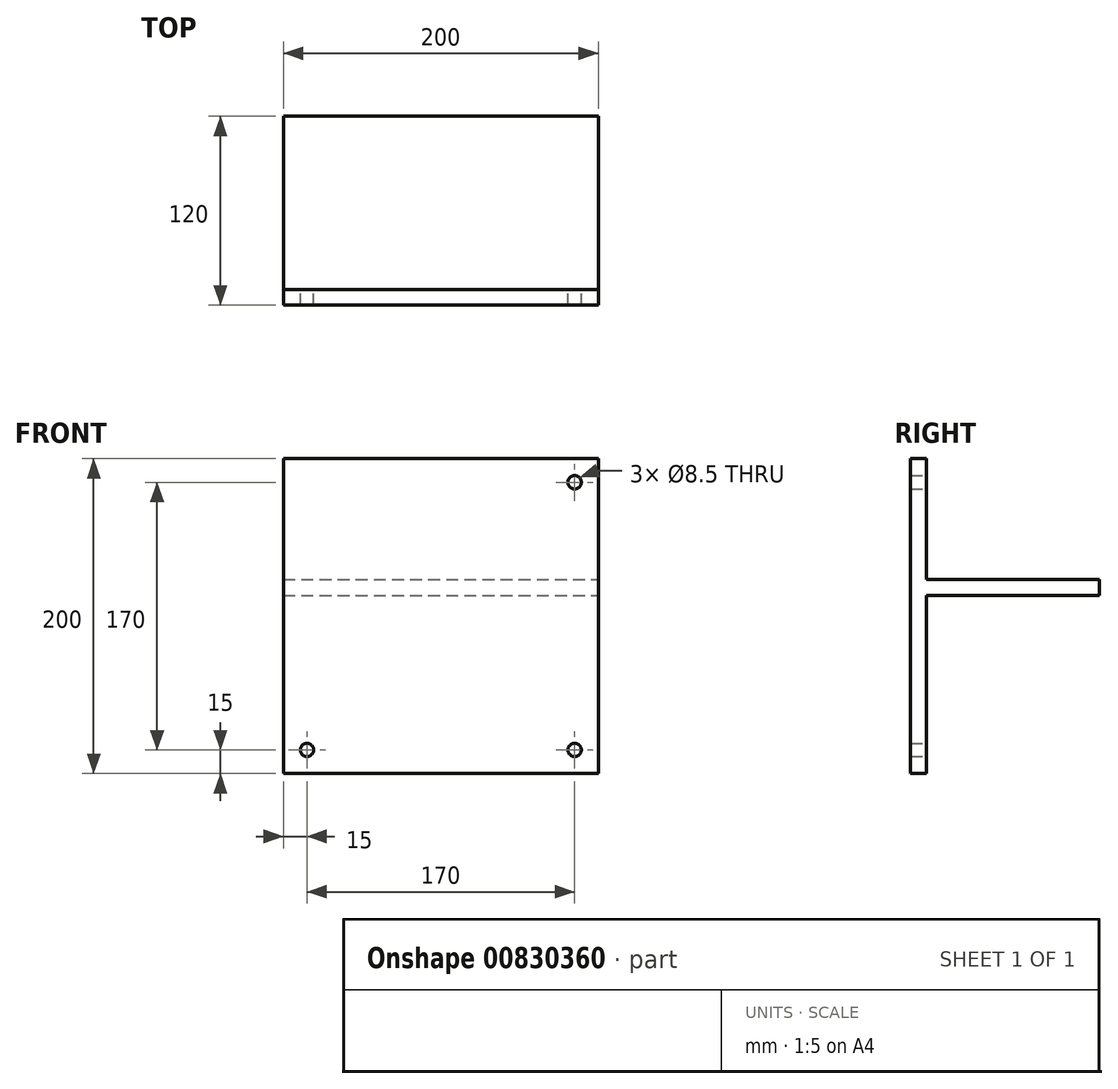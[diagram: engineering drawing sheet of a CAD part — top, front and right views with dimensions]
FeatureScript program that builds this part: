
annotation { "Feature Type Name" : "Feature", "Feature Type Description" : "" }
export const myFeature = defineFeature(function(context is Context, id is Id, definition is map)
    precondition{}
    {
        {
            var Q0;
            Q0=qCreatedBy(makeId("Front.planeOp"),FACE);
            var sketch = newSketch(context, id + "F0", { "sketchPlane" : qUnion([Q0])});
            skLineSegment(sketch, "E0.bottom", {"start": v(-100, 100) * mm, "end": v(100, 100) * mm});
            skLineSegment(sketch, "E0.top", {"start": v(-100, -100) * mm, "end": v(100, -100) * mm});
            skLineSegment(sketch, "E0.left", {"start": v(-100, 100) * mm, "end": v(-100, -100) * mm});
            skLineSegment(sketch, "E0.right", {"start": v(100, 100) * mm, "end": v(100, -100) * mm});
            skPoint(sketch, "E0.middle", {"position": v(0, 0) * mm});
            skSolve(sketch);
        }
        {
            var Q0;
            Q0=makeQuery(id+"F0.imprint","IMPRINT",FACE,{"disambiguationData":[TD([[makeQuery(id+"F0.imprint","IMPRINT",EDGE,{"derivedFrom":sQuery(id+"F0.wireOp",EDGE,"E0.bottom")}),-1.0]])]});
            extrude(context, id + "F1", {"entities" : qUnion([Q0]), "depth" : 120 * mm, "offsetDistance" : 25 * mm});
        }
        {
            var Q0;
            Q0=makeQuery(id+"F1.opExtrude","SWEPT_FACE",FACE,{"disambiguationData":[OSD([sQuery(id+"F0.wireOp",EDGE,"E0.right")])]});
            var sketch = newSketch(context, id + "F2", { "sketchPlane" : qUnion([Q0])});
            skLineSegment(sketch, "E1", {"start": v(-110, 100) * mm, "end": v(-110, -100) * mm});
            skLineSegment(sketch, "E2", {"start": v(-110, 23.2) * mm, "end": v(0, 23.2) * mm});
            skLineSegment(sketch, "E3", {"start": v(-110, 13.2) * mm, "end": v(0, 13.2) * mm});
            skSolve(sketch);
        }
        {
            var Q0;
            {var subQ4=sQuery(id+"F2.wireOp",EDGE,"E2");Q0=makeQuery(id+"F2.imprint","IMPRINT",FACE,{"disambiguationData":[TD([[makeQuery(id+"F2.imprint","IMPRINT",EDGE,{"derivedFrom":subQ4}),1.0]])]});}
            var Q1;
            {var subQ4=sQuery(id+"F2.wireOp",EDGE,"E3");Q1=makeQuery(id+"F2.imprint","IMPRINT",FACE,{"disambiguationData":[TD([[makeQuery(id+"F2.imprint","IMPRINT",EDGE,{"derivedFrom":subQ4}),-1.0]])]});}
            extrude(context, id + "F3", {"entities" : qUnion([Q0, Q1]), "operationType" : NewBodyOperationType.REMOVE, "oppositeDirection" : true, "depth" : 200 * mm, "offsetDistance" : 25 * mm});
        }
        {
            var Q0;
            {var subQ0=sQuery(id+"F2.wireOp",EDGE,"E1");Q0=makeQuery(id+"F3.boolean.opBoolean","COPY",FACE,{"derivedFrom":makeQuery(id+"F3.opExtrude","SWEPT_FACE",FACE,{"disambiguationData":[OSD([subQ0]),TDD([makeQuery(id+"F2.imprint","IMPRINT",EDGE,{"disambiguationData":[TD([[makeQuery(id+"F2.imprint","INTERSECT",VERTEX,{"derivedFrom":[subQ0,sQuery(id+"F2.wireOp",EDGE,"E3")]}),-1.0]])],"derivedFrom":subQ0})])]})});}
            var sketch = newSketch(context, id + "F4", { "sketchPlane" : qUnion([Q0])});
            skLineSegment(sketch, "E4", {"start": v(-5, 13.2) * mm, "end": v(-5, -100) * mm});
            skLineSegment(sketch, "E5", {"start": v(5, 13.2) * mm, "end": v(5, -100) * mm});
            skSolve(sketch);
        }
        {
            var Q0;
            {var subQ0=sQuery(id+"F4.wireOp",EDGE,"E4");Q0=makeQuery(id+"F4.imprint","IMPRINT",FACE,{"disambiguationData":[TD([[makeQuery(id+"F4.imprint","IMPRINT",EDGE,{"derivedFrom":subQ0}),-1.0]])]});}
            var sketch = newSketch(context, id + "F5", { "sketchPlane" : qUnion([Q0])});
            skCircle(sketch, "E6", {"center": v(-85, 85) * mm, "radius": 4.25 * mm});
            skCircle(sketch, "E7.MirrorC", {"center": v(85, 85) * mm, "radius": 4.25 * mm});
            skSolve(sketch);
        }
        {
            var Q0;
            Q0=makeQuery(id+"F5.imprint","IMPRINT",FACE,{"disambiguationData":[TD([[makeQuery(id+"F5.imprint","IMPRINT",EDGE,{"derivedFrom":sQuery(id+"F5.wireOp",EDGE,"E6")}),1.0]])]});
            var Q1;
            Q1=makeQuery(id+"F5.imprint","IMPRINT",FACE,{"disambiguationData":[TD([[makeQuery(id+"F5.imprint","IMPRINT",EDGE,{"derivedFrom":sQuery(id+"F5.wireOp",EDGE,"E7.MirrorC")}),-1.0]])]});
            extrude(context, id + "F6", {"entities" : qUnion([Q0, Q1]), "operationType" : NewBodyOperationType.REMOVE, "oppositeDirection" : true, "depth" : 10 * mm, "offsetDistance" : 25 * mm});
        }
        {
            var Q0;
            {var subQ0=sQuery(id+"F4.wireOp",EDGE,"E4");Q0=makeQuery(id+"F4.imprint","IMPRINT",FACE,{"disambiguationData":[TD([[makeQuery(id+"F4.imprint","IMPRINT",EDGE,{"derivedFrom":subQ0}),-1.0]])]});}
            var sketch = newSketch(context, id + "F7", { "sketchPlane" : qUnion([Q0])});
            skCircle(sketch, "E8", {"center": v(-85, -85) * mm, "radius": 4.25 * mm});
            skSolve(sketch);
        }
        {
            var Q0;
            Q0 = qSketchRegion(id + "F7", true);
            extrude(context, id + "F8", {"entities" : qUnion([Q0]), "operationType" : NewBodyOperationType.REMOVE, "oppositeDirection" : true, "depth" : 10 * mm, "offsetDistance" : 25 * mm});
        }
        {
            var Q0;
            {var subQ0=sQuery(id+"F4.wireOp",EDGE,"E5");Q0=makeQuery(id+"F4.imprint","IMPRINT",FACE,{"disambiguationData":[TD([[makeQuery(id+"F4.imprint","IMPRINT",EDGE,{"derivedFrom":subQ0}),1.0]])]});}
            var sketch = newSketch(context, id + "F9", { "sketchPlane" : qUnion([Q0])});
            skCircle(sketch, "E9", {"center": v(85, -85) * mm, "radius": 4.25 * mm});
            skSolve(sketch);
        }
        {
            var Q0;
            Q0 = qSketchRegion(id + "F9", true);
            extrude(context, id + "F10", {"entities" : qUnion([Q0]), "operationType" : NewBodyOperationType.REMOVE, "oppositeDirection" : true, "depth" : 10 * mm, "offsetDistance" : 25 * mm});
        }
    });
